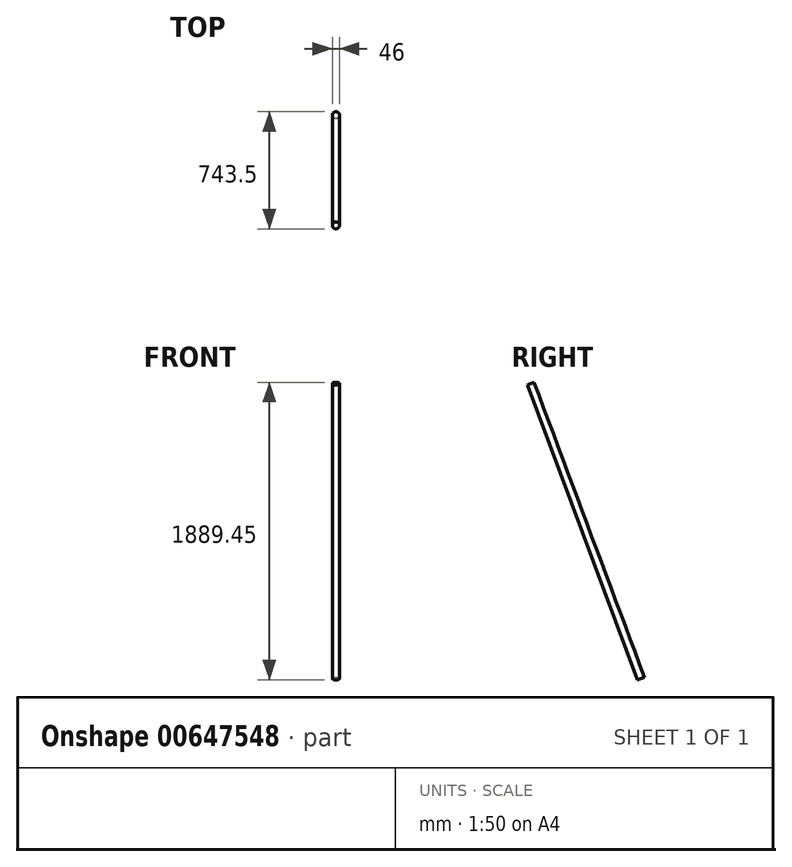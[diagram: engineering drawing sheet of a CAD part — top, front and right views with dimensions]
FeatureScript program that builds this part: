
annotation { "Feature Type Name" : "Feature", "Feature Type Description" : "" }
export const myFeature = defineFeature(function(context is Context, id is Id, definition is map)
    precondition{}
    {
        {
            var Q0;
            Q0=qCreatedBy(makeId("Right.planeOp"),FACE);
            var sketch = newSketch(context, id + "F0", { "sketchPlane" : qUnion([Q0])});
            skLineSegment(sketch, "E0", {"start": v(-74.65, 0) * mm, "end": v(75.73, 0) * mm, "construction": true});
            skLineSegment(sketch, "E1", {"start": v(0, 0) * mm, "end": v(-22.75, 60.86) * mm});
            skLineSegment(sketch, "E2", {"start": v(0, 0) * mm, "end": v(-63.16, -23.61) * mm});
            skSolve(sketch);
        }
        {
            var Q0;
            Q0=sQuery(id+"F0.wireOp",EDGE,"E2");
            cPlane(context, id + "F1", {"entities" : qUnion([Q0]), "cplaneType" : CPlaneType.LINE_ANGLE, "offset" : 25 * mm, "angle" : 0 * degree, "width" : 150 * mm, "height" : 150 * mm});
        }
        {
            var Q0;
            Q0=qCreatedBy(id+"F1.planeOp",FACE);
            var sketch = newSketch(context, id + "F2", { "sketchPlane" : qUnion([Q0])});
            skCircle(sketch, "E3", {"center": v(0, 0) * mm, "radius": 23 * mm});
            skSolve(sketch);
        }
        {
            var Q0;
            Q0=makeQuery(id+"F2.imprint","IMPRINT",FACE,{"disambiguationData":[TD([[makeQuery(id+"F2.imprint","IMPRINT",EDGE,{"derivedFrom":sQuery(id+"F2.wireOp",EDGE,"E3")}),1.0]])]});
            extrude(context, id + "F3", {"entities" : qUnion([Q0]), "oppositeDirection" : true, "depth" : 2000 * mm, "offsetDistance" : 25 * mm});
        }
    });
